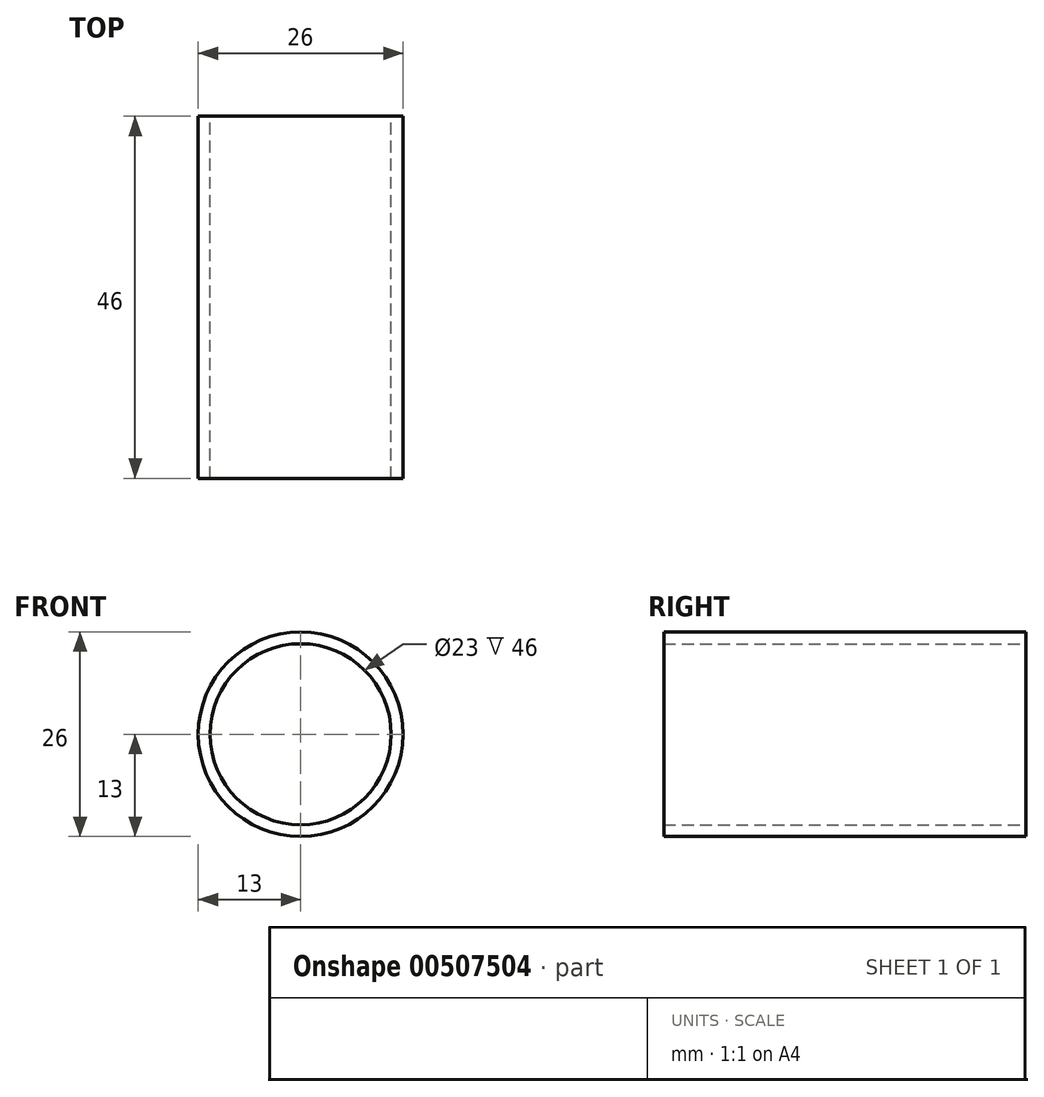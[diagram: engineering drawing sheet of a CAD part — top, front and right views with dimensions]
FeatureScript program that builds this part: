
annotation { "Feature Type Name" : "Feature", "Feature Type Description" : "" }
export const myFeature = defineFeature(function(context is Context, id is Id, definition is map)
    precondition{}
    {
        {
            var Q0;
            Q0=qCreatedBy(makeId("Front.planeOp"),FACE);
            var sketch = newSketch(context, id + "F0", { "sketchPlane" : qUnion([Q0])});
            skCircle(sketch, "E0", {"center": v(0, 0) * mm, "radius": 13 * mm});
            skCircle(sketch, "E1", {"center": v(0, 0) * mm, "radius": 11.5 * mm});
            skSolve(sketch);
        }
        {
            var Q0;
            Q0 = qSketchRegion(id + "F0", true);
            extrude(context, id + "F1", {"entities" : qUnion([Q0]), "depth" : 46 * mm});
        }
    });
